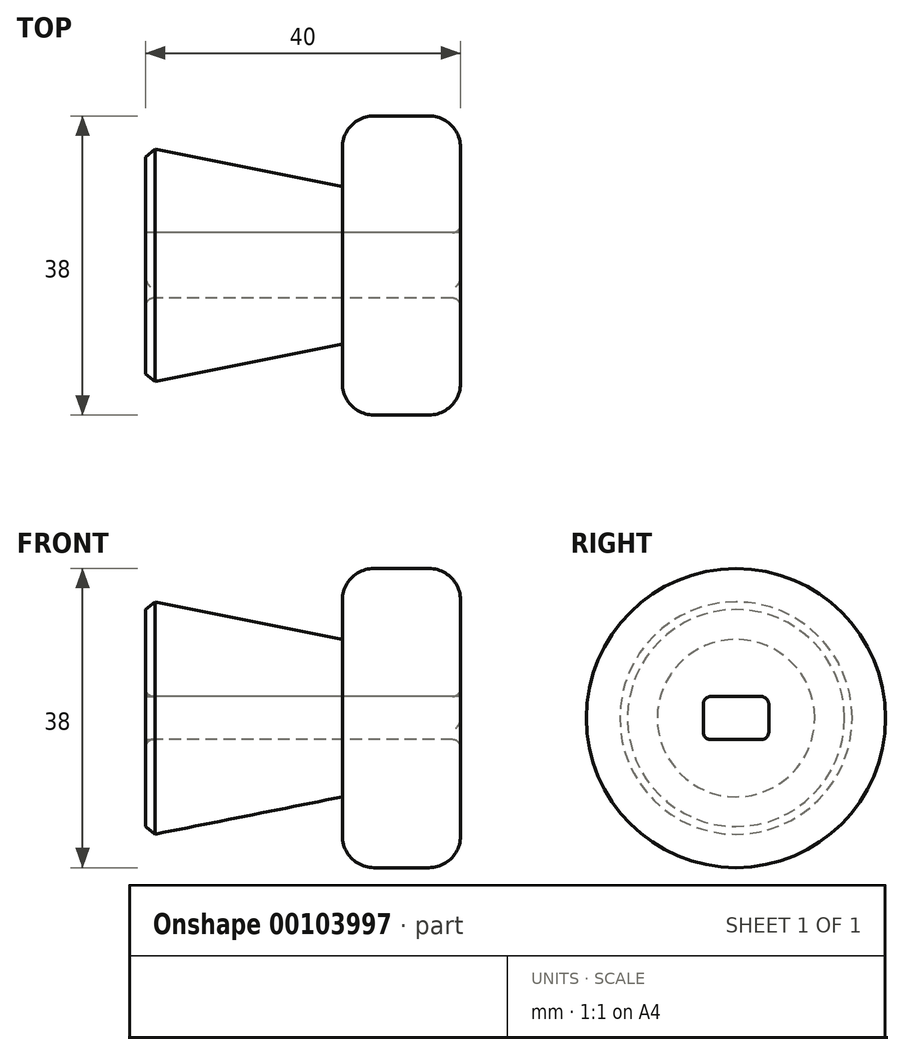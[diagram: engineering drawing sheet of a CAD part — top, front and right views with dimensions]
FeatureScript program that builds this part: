
annotation { "Feature Type Name" : "Feature", "Feature Type Description" : "" }
export const myFeature = defineFeature(function(context is Context, id is Id, definition is map)
    precondition{}
    {
        {
            var Q0;
            Q0=qCreatedBy(makeId("Front.planeOp"),FACE);
            var sketch = newSketch(context, id + "F0", { "sketchPlane" : qUnion([Q0])});
            skLineSegment(sketch, "E0", {"start": v(0, 0) * mm, "end": v(0, 15) * mm});
            skLineSegment(sketch, "E1", {"start": v(0, 15) * mm, "end": v(25, 10) * mm});
            skLineSegment(sketch, "E2", {"start": v(25, 10) * mm, "end": v(25, 15) * mm});
            skLineSegment(sketch, "E3", {"start": v(29, 19) * mm, "end": v(36, 19) * mm});
            skLineSegment(sketch, "E4", {"start": v(40, 15) * mm, "end": v(40, 0) * mm});
            skLineSegment(sketch, "E5", {"start": v(40, 0) * mm, "end": v(0, 0) * mm, "construction": true});
            skPoint(sketch, "E6.visualSharp", {"position": v(25, 19) * mm});
            skArc(sketch, "E6.filletArc", {"start": v(29, 19) * mm, "mid": v(26.17, 17.83) * mm, "end": v(25, 15) * mm});
            skPoint(sketch, "E7.visualSharp", {"position": v(40, 19) * mm});
            skArc(sketch, "E7.filletArc", {"start": v(40, 15) * mm, "mid": v(38.83, 17.83) * mm, "end": v(36, 19) * mm});
            skLineSegment(sketch, "E8", {"start": v(0, 0) * mm, "end": v(40, 0) * mm});
            skSolve(sketch);
        }
        {
            var Q0;
            Q0 = qSketchRegion(id + "F0", true);
            var Q1;
            Q1=sQuery(id+"F0.wireOp",EDGE,"E5");
            revolve(context, id + "F1", {"entities" : qUnion([Q0]), "axis" : qUnion([Q1]), "revolveType" : RevolveType.FULL});
        }
        {
            var Q0;
            Q0=makeQuery(id+"F1.opRevolve","SWEPT_FACE",FACE,{"disambiguationData":[OSD([sQuery(id+"F0.wireOp",EDGE,"E0")])]});
            var sketch = newSketch(context, id + "F2", { "sketchPlane" : qUnion([Q0])});
            skLineSegment(sketch, "E9.bottom", {"start": v(4.16, 2.74) * mm, "end": v(-4.16, 2.74) * mm});
            skLineSegment(sketch, "E9.top", {"start": v(4.16, -2.74) * mm, "end": v(-4.16, -2.74) * mm});
            skLineSegment(sketch, "E9.left", {"start": v(4.16, 2.74) * mm, "end": v(4.16, -2.74) * mm});
            skLineSegment(sketch, "E9.right", {"start": v(-4.16, 2.74) * mm, "end": v(-4.16, -2.74) * mm});
            skPoint(sketch, "E9.middle", {"position": v(0, 0) * mm});
            skSolve(sketch);
        }
        {
            var Q0;
            Q0 = qSketchRegion(id + "F2", true);
            extrude(context, id + "F3", {"entities" : qUnion([Q0]), "operationType" : NewBodyOperationType.REMOVE, "endBound" : BoundingType.THROUGH_ALL, "oppositeDirection" : true, "depth" : 25 * mm});
        }
        {
            var Q0;
            Q0=makeQuery(id+"F1.opRevolve","SWEPT_EDGE",EDGE,{"disambiguationData":[OSD([sQuery(id+"F0.wireOp",EDGE,"E0"),sQuery(id+"F0.wireOp",EDGE,"E1")])]});
            chamfer(context, id + "F4", {"entities" : qUnion([Q0]), "width" : 1 * mm, "tangentPropagation" : true});
        }
        {
            var Q0;
            Q0=makeQuery(id+"F3.boolean.opBoolean","COPY",FACE,{"derivedFrom":makeQuery(id+"F3.opExtrude","SWEPT_FACE",FACE,{"disambiguationData":[OSD([sQuery(id+"F2.wireOp",EDGE,"E9.left")])]})});
            var Q1;
            Q1=makeQuery(id+"F3.boolean.opBoolean","INTERSECT",EDGE,{"derivedFrom":[makeQuery(id+"F1.opRevolve","SWEPT_FACE",FACE,{"disambiguationData":[OSD([sQuery(id+"F0.wireOp",EDGE,"E4")])]}),makeQuery(id+"F3.opExtrude","SWEPT_FACE",FACE,{"disambiguationData":[OSD([sQuery(id+"F2.wireOp",EDGE,"E9.top")])]})]});
            var Q2;
            Q2=makeQuery(id+"F3.boolean.opBoolean","COPY",EDGE,{"derivedFrom":makeQuery(id+"F3.opExtrude","CAP_EDGE",EDGE,{"disambiguationData":[OSD([sQuery(id+"F2.wireOp",EDGE,"E9.right")])],"isStart":true})});
            var Q3;
            Q3=makeQuery(id+"F3.boolean.opBoolean","COPY",EDGE,{"derivedFrom":makeQuery(id+"F3.opExtrude","SWEPT_EDGE",EDGE,{"disambiguationData":[OSD([sQuery(id+"F2.wireOp",EDGE,"E9.top"),sQuery(id+"F2.wireOp",EDGE,"E9.left")])]})});
            var Q4;
            Q4=makeQuery(id+"F3.boolean.opBoolean","COPY",EDGE,{"derivedFrom":makeQuery(id+"F3.opExtrude","SWEPT_EDGE",EDGE,{"disambiguationData":[OSD([sQuery(id+"F2.wireOp",EDGE,"E9.bottom"),sQuery(id+"F2.wireOp",EDGE,"E9.left")])]})});
            var Q5;
            Q5=makeQuery(id+"F3.boolean.opBoolean","COPY",EDGE,{"derivedFrom":makeQuery(id+"F3.opExtrude","SWEPT_EDGE",EDGE,{"disambiguationData":[OSD([sQuery(id+"F2.wireOp",EDGE,"E9.bottom"),sQuery(id+"F2.wireOp",EDGE,"E9.right")])]})});
            var Q6;
            Q6=makeQuery(id+"F3.boolean.opBoolean","COPY",EDGE,{"derivedFrom":makeQuery(id+"F3.opExtrude","SWEPT_EDGE",EDGE,{"disambiguationData":[OSD([sQuery(id+"F2.wireOp",EDGE,"E9.top"),sQuery(id+"F2.wireOp",EDGE,"E9.right")])]})});
            fillet(context, id + "F5", {"entities" : qUnion([Q0, Q1, Q2, Q3, Q4, Q5, Q6]), "radius" : 1 * mm, "tangentPropagation" : true, "allowEdgeOverflow" : false});
        }
    });
